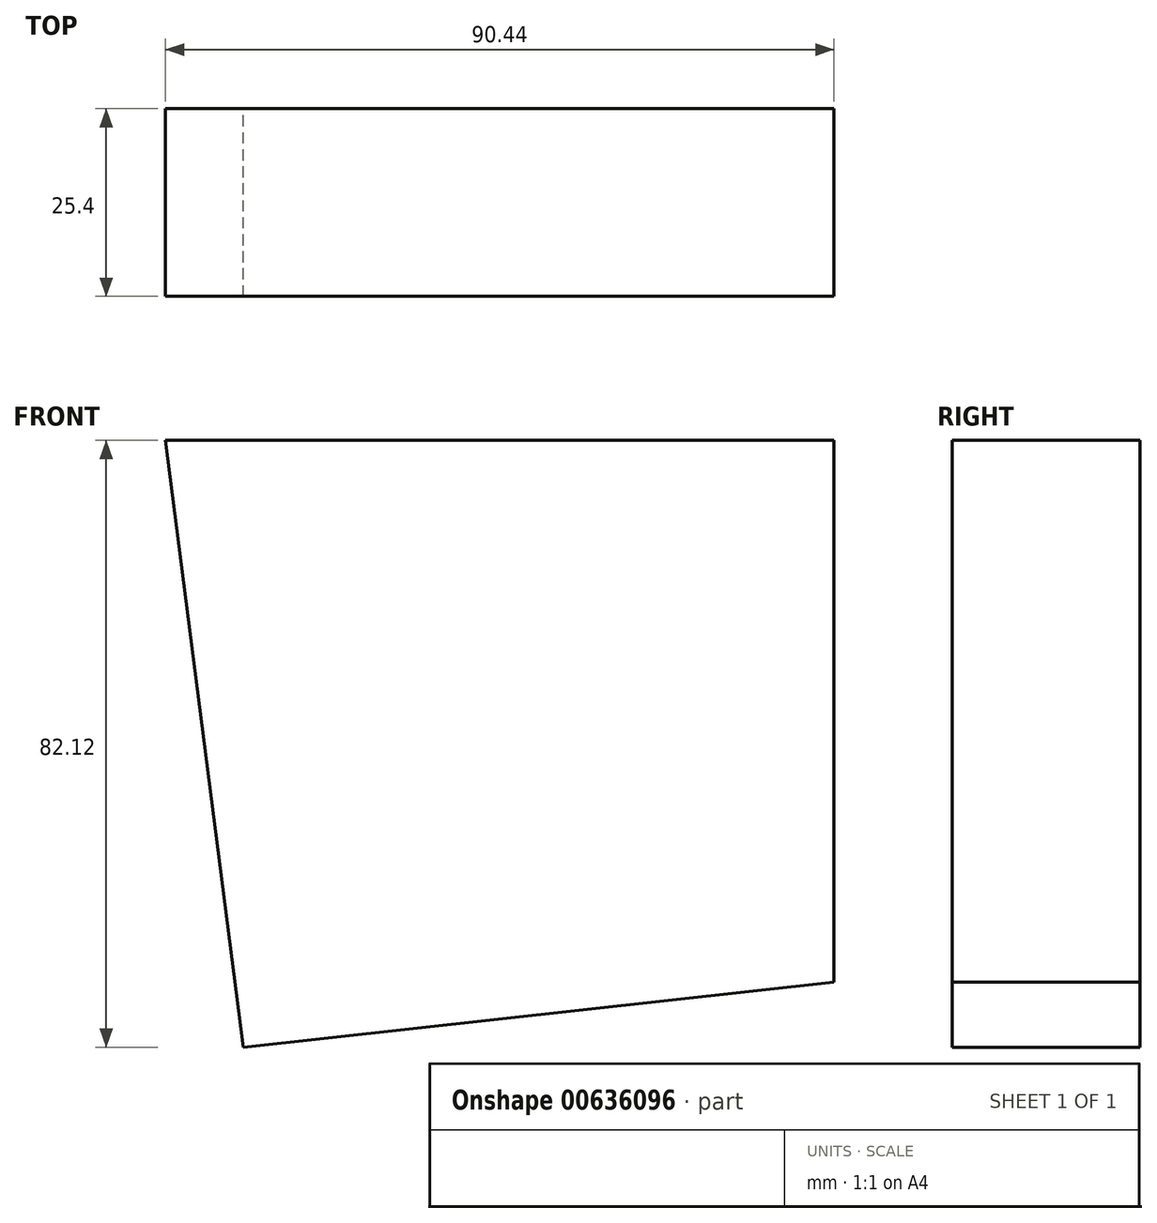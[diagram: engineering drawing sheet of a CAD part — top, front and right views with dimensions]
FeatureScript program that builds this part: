
annotation { "Feature Type Name" : "Feature", "Feature Type Description" : "" }
export const myFeature = defineFeature(function(context is Context, id is Id, definition is map)
    precondition{}
    {
        {
            var Q0;
            Q0=qCreatedBy(makeId("Front.planeOp"),FACE);
            var sketch = newSketch(context, id + "F0", { "sketchPlane" : qUnion([Q0])});
            skLineSegment(sketch, "E0", {"start": v(-43.02, 37.64) * mm, "end": v(47.42, 37.64) * mm});
            skLineSegment(sketch, "E1", {"start": v(47.42, 37.64) * mm, "end": v(47.42, -35.68) * mm});
            skLineSegment(sketch, "E2", {"start": v(47.42, -35.68) * mm, "end": v(-32.5, -44.48) * mm});
            skLineSegment(sketch, "E3", {"start": v(-32.5, -44.48) * mm, "end": v(-43.02, 37.64) * mm});
            skSolve(sketch);
        }
        {
            var Q0;
            Q0=makeQuery(id+"F0.imprint","IMPRINT",FACE,{"disambiguationData":[TD([[makeQuery(id+"F0.imprint","IMPRINT",EDGE,{"derivedFrom":sQuery(id+"F0.wireOp",EDGE,"E0")}),-1.0]])]});
            extrude(context, id + "F1", {"entities" : qUnion([Q0]), "depth" : 25.4 * mm, "offsetDistance" : 25.4 * mm});
        }
    });
